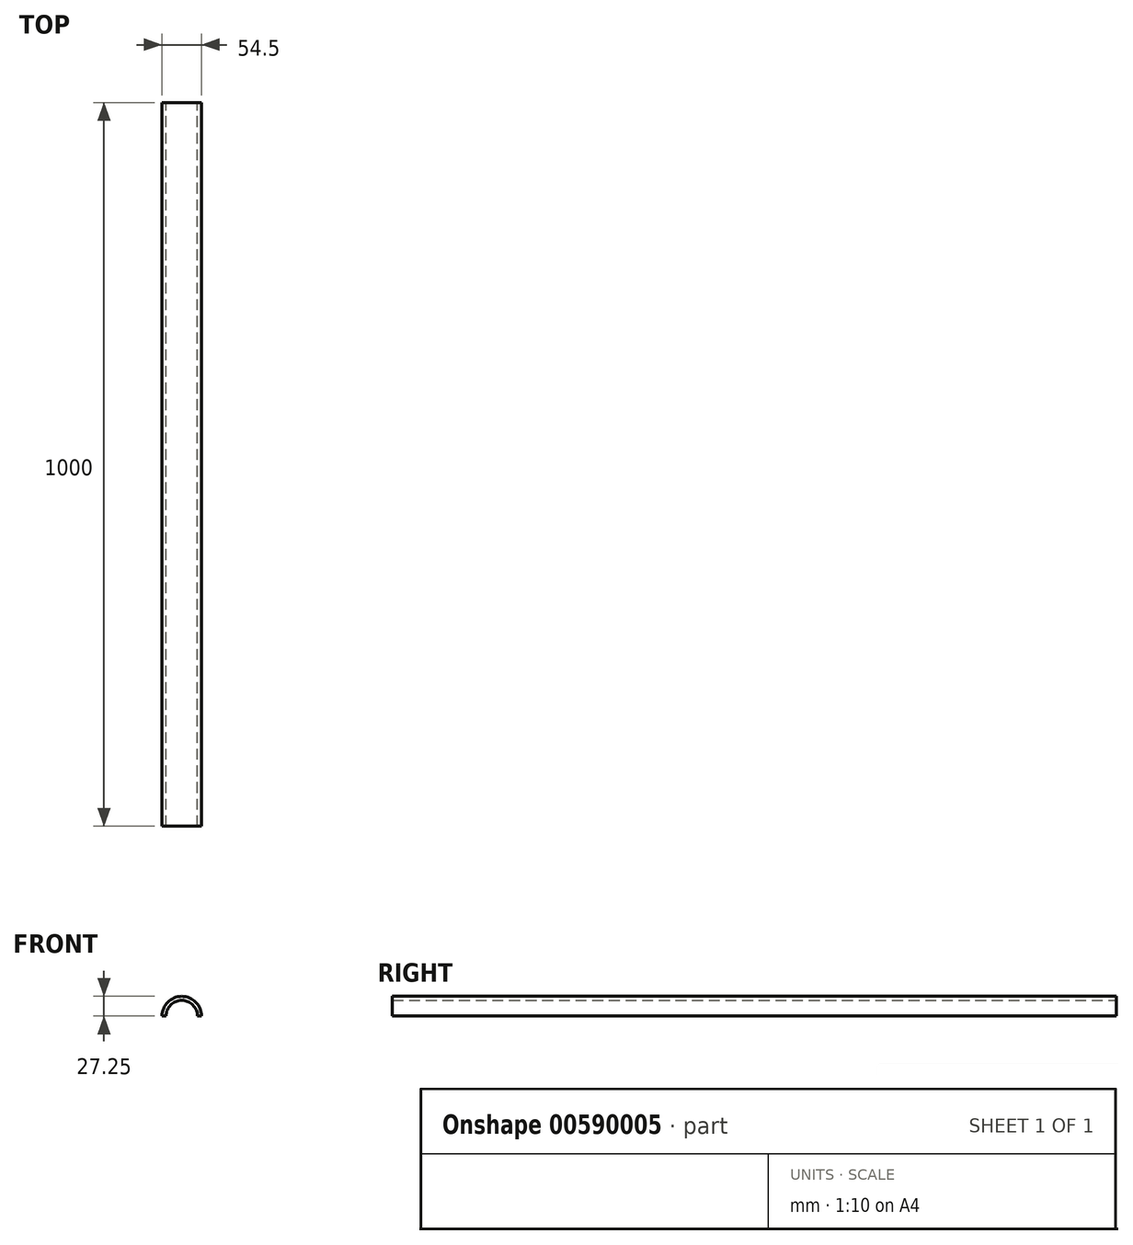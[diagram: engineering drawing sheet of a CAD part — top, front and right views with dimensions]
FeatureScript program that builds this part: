
annotation { "Feature Type Name" : "Feature", "Feature Type Description" : "" }
export const myFeature = defineFeature(function(context is Context, id is Id, definition is map)
    precondition{}
    {
        {
            var Q0;
            Q0=qCreatedBy(makeId("Front.planeOp"),FACE);
            var sketch = newSketch(context, id + "F0", { "sketchPlane" : qUnion([Q0])});
            skArc(sketch, "E0", {"start": v(21.7, 0) * mm, "mid": v(0, 21.7) * mm, "end": v(-21.7, 0) * mm});
            skArc(sketch, "E1", {"start": v(27.25, 0) * mm, "mid": v(0, 27.25) * mm, "end": v(-27.25, 0) * mm});
            skLineSegment(sketch, "E2", {"start": v(-27.25, 0) * mm, "end": v(-21.7, 0) * mm});
            skLineSegment(sketch, "E3", {"start": v(27.25, 0) * mm, "end": v(21.7, 0) * mm});
            skSolve(sketch);
        }
        {
            var Q0;
            Q0=makeQuery(id+"F0.imprint","IMPRINT",FACE,{"disambiguationData":[TD([[makeQuery(id+"F0.imprint","IMPRINT",EDGE,{"derivedFrom":sQuery(id+"F0.wireOp",EDGE,"E0")}),-1.0]])]});
            extrude(context, id + "F1", {"entities" : qUnion([Q0]), "depth" : 1000 * mm, "offsetDistance" : 25 * mm});
        }
        {
            var Q0;
            Q0=makeQuery(id+"F1.opExtrude","CAP_FACE",FACE,{"disambiguationData":[OSD([sQuery(id+"F0.wireOp",EDGE,"E0"),sQuery(id+"F0.wireOp",EDGE,"E1"),sQuery(id+"F0.wireOp",EDGE,"E2"),sQuery(id+"F0.wireOp",EDGE,"E3")])],"isStart":true});
            var sketch = newSketch(context, id + "F2", { "sketchPlane" : qUnion([Q0])});
            skCircle(sketch, "E4", {"center": v(0, 0) * mm, "radius": 27.06 * mm});
            skSolve(sketch);
        }
        {
            var Q0;
            {var subQ5=makeQuery(id+"F1.opExtrude","CAP_EDGE",EDGE,{"disambiguationData":[OSD([sQuery(id+"F0.wireOp",EDGE,"E0")])],"isStart":true});Q0=makeQuery(id+"F2.imprint","IMPRINT",FACE,{"disambiguationData":[TD([[makeQuery(id+"F2.imprint","IMPRINT",EDGE,{"derivedFrom":subQ5}),-1.0]])]});}
            var sketch = newSketch(context, id + "F3", { "sketchPlane" : qUnion([Q0])});
            skCircle(sketch, "E5", {"center": v(0, 0) * mm, "radius": 6 * mm});
            skSolve(sketch);
        }
        {
            var Q0;
            Q0=sQuery(id+"F3.wireOp",EDGE,"E5");
            extrude(context, id + "F4", {"bodyType" : ToolBodyType.SURFACE, "surfaceEntities" : qUnion([Q0]), "oppositeDirection" : true, "depth" : 1000 * mm, "offsetDistance" : 25 * mm});
        }
    });
